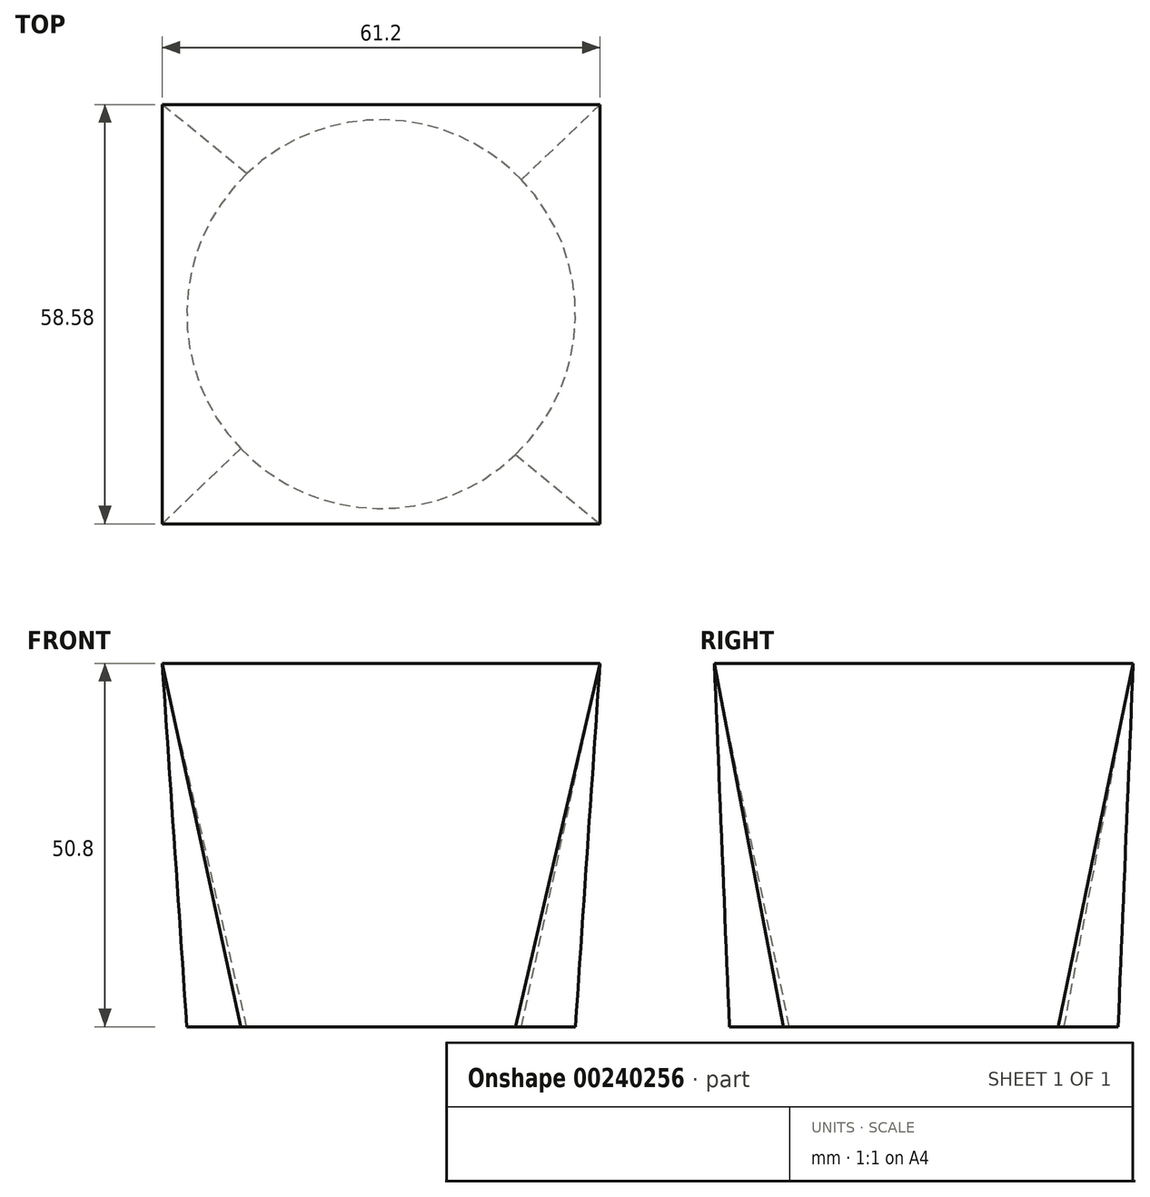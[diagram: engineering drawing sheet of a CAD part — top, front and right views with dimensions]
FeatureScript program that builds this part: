
annotation { "Feature Type Name" : "Feature", "Feature Type Description" : "" }
export const myFeature = defineFeature(function(context is Context, id is Id, definition is map)
    precondition{}
    {
        {
            var Q0;
            Q0=qCreatedBy(makeId("Top.planeOp"),FACE);
            var sketch = newSketch(context, id + "F0", { "sketchPlane" : qUnion([Q0])});
            skCircle(sketch, "E0", {"center": v(0, 0) * mm, "radius": 27.17 * mm});
            skSolve(sketch);
        }
        {
            var Q0;
            Q0=qCreatedBy(makeId("Top.planeOp"),FACE);
            cPlane(context, id + "F1", {"entities" : qUnion([Q0]), "cplaneType" : CPlaneType.OFFSET, "offset" : 50.8 * mm, "width" : 152.4 * mm, "height" : 152.4 * mm});
        }
        {
            var Q0;
            Q0=qCreatedBy(id+"F1.planeOp",FACE);
            var sketch = newSketch(context, id + "F2", { "sketchPlane" : qUnion([Q0])});
            skLineSegment(sketch, "E1.bottom", {"start": v(30.6, 29.3) * mm, "end": v(-30.6, 29.3) * mm});
            skLineSegment(sketch, "E1.top", {"start": v(30.6, -29.3) * mm, "end": v(-30.6, -29.3) * mm});
            skLineSegment(sketch, "E1.left", {"start": v(30.6, 29.3) * mm, "end": v(30.6, -29.3) * mm});
            skLineSegment(sketch, "E1.right", {"start": v(-30.6, 29.3) * mm, "end": v(-30.6, -29.3) * mm});
            skPoint(sketch, "E1.middle", {"position": v(0, 0) * mm});
            skSolve(sketch);
        }
        {
            var Q0;
            Q0=makeQuery(id+"F0.imprint","IMPRINT",FACE,{"disambiguationData":[TD([[makeQuery(id+"F0.imprint","IMPRINT",EDGE,{"derivedFrom":sQuery(id+"F0.wireOp",EDGE,"E0")}),1.0]])]});
            var Q1;
            Q1=makeQuery(id+"F2.imprint","IMPRINT",FACE,{"disambiguationData":[TD([[makeQuery(id+"F2.imprint","IMPRINT",EDGE,{"derivedFrom":sQuery(id+"F2.wireOp",EDGE,"E1.bottom")}),1.0]])]});
            loft(context, id + "F3", {"sheetProfilesArray" : [{ "sheetProfileEntities" : qUnion([Q0]) }, { "sheetProfileEntities" : qUnion([Q1]) }]});
        }
    });
